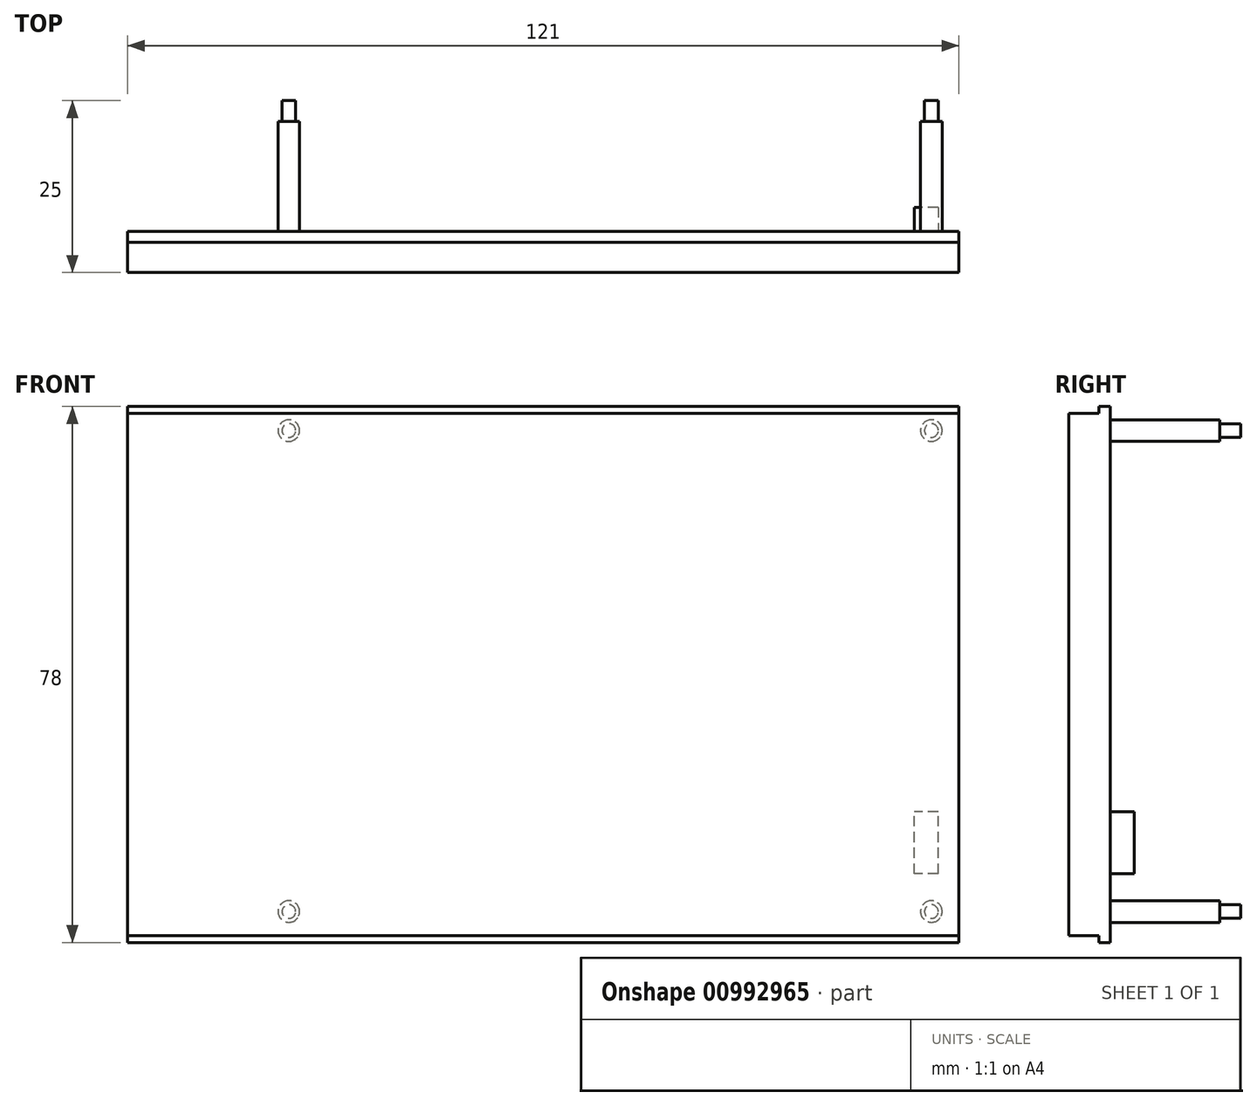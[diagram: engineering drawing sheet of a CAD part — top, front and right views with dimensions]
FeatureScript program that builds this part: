
annotation { "Feature Type Name" : "Feature", "Feature Type Description" : "" }
export const myFeature = defineFeature(function(context is Context, id is Id, definition is map)
    precondition{}
    {
        {
            var Q0;
            Q0=qCreatedBy(makeId("Front.planeOp"),FACE);
            var sketch = newSketch(context, id + "F0", { "sketchPlane" : qUnion([Q0])});
            skLineSegment(sketch, "E0.bottom", {"start": v(60.5, 38) * mm, "end": v(-60.5, 38) * mm});
            skLineSegment(sketch, "E0.top", {"start": v(60.5, -38) * mm, "end": v(-60.5, -38) * mm});
            skLineSegment(sketch, "E0.left", {"start": v(60.5, 38) * mm, "end": v(60.5, -38) * mm});
            skLineSegment(sketch, "E0.right", {"start": v(-60.5, 38) * mm, "end": v(-60.5, -38) * mm});
            skPoint(sketch, "E0.middle", {"position": v(0, 0) * mm});
            skSolve(sketch);
        }
        {
            var Q0;
            Q0=makeQuery(id+"F0.imprint","IMPRINT",FACE,{"disambiguationData":[TD([[makeQuery(id+"F0.imprint","IMPRINT",EDGE,{"derivedFrom":sQuery(id+"F0.wireOp",EDGE,"E0.bottom")}),1.0]])]});
            extrude(context, id + "F1", {"entities" : qUnion([Q0]), "depth" : 6 * mm, "offsetDistance" : 25.4 * mm});
        }
        {
            var Q0;
            Q0=qCreatedBy(makeId("Front.planeOp"),FACE);
            var sketch = newSketch(context, id + "F2", { "sketchPlane" : qUnion([Q0])});
            skLineSegment(sketch, "E1.bottom", {"start": v(-60.5, 39) * mm, "end": v(60.5, 39) * mm});
            skLineSegment(sketch, "E1.top", {"start": v(-60.5, -39) * mm, "end": v(60.5, -39) * mm});
            skLineSegment(sketch, "E1.left", {"start": v(-60.5, 39) * mm, "end": v(-60.5, -39) * mm});
            skLineSegment(sketch, "E1.right", {"start": v(60.5, 39) * mm, "end": v(60.5, -39) * mm});
            skPoint(sketch, "E1.middle", {"position": v(0, 0) * mm});
            skSolve(sketch);
        }
        {
            var Q0;
            Q0=makeQuery(id+"F2.imprint","IMPRINT",FACE,{"disambiguationData":[TD([[makeQuery(id+"F2.imprint","IMPRINT",EDGE,{"derivedFrom":sQuery(id+"F2.wireOp",EDGE,"E1.bottom")}),-1.0]])]});
            extrude(context, id + "F3", {"entities" : qUnion([Q0]), "operationType" : NewBodyOperationType.ADD, "depth" : 1.6 * mm, "offsetDistance" : 25.4 * mm});
        }
        {
            var Q0;
            Q0=makeQuery(id+"F3.boolean.opBoolean","MERGE",FACE,{"derivedFrom":[makeQuery(id+"F1.opExtrude","CAP_FACE",FACE,{"disambiguationData":[OSD([sQuery(id+"F0.wireOp",EDGE,"E0.bottom"),sQuery(id+"F0.wireOp",EDGE,"E0.top"),sQuery(id+"F0.wireOp",EDGE,"E0.left"),sQuery(id+"F0.wireOp",EDGE,"E0.right")])],"isStart":true}),makeQuery(id+"F3.opExtrude","CAP_FACE",FACE,{"disambiguationData":[OSD([sQuery(id+"F2.wireOp",EDGE,"E1.bottom"),sQuery(id+"F2.wireOp",EDGE,"E1.top"),sQuery(id+"F2.wireOp",EDGE,"E1.left"),sQuery(id+"F2.wireOp",EDGE,"E1.right")])],"isStart":true})]});
            var sketch = newSketch(context, id + "F4", { "sketchPlane" : qUnion([Q0])});
            skCircle(sketch, "E2", {"center": v(-56.5, 35.5) * mm, "radius": 1 * mm});
            skCircle(sketch, "E3", {"center": v(-56.5, -34.5) * mm, "radius": 1 * mm});
            skCircle(sketch, "E4", {"center": v(37, -34.5) * mm, "radius": 1 * mm});
            skCircle(sketch, "E5", {"center": v(37, 35.5) * mm, "radius": 1 * mm});
            skSolve(sketch);
        }
        {
            var Q0;
            Q0 = qSketchRegion(id + "F4", true);
            extrude(context, id + "F5", {"entities" : qUnion([Q0]), "operationType" : NewBodyOperationType.ADD, "depth" : 2 * mm, "offsetDistance" : 25.4 * mm});
        }
        {
            var Q0;
            Q0=makeQuery(id+"F3.boolean.opBoolean","MERGE",FACE,{"derivedFrom":[makeQuery(id+"F1.opExtrude","CAP_FACE",FACE,{"disambiguationData":[OSD([sQuery(id+"F0.wireOp",EDGE,"E0.bottom"),sQuery(id+"F0.wireOp",EDGE,"E0.top"),sQuery(id+"F0.wireOp",EDGE,"E0.left"),sQuery(id+"F0.wireOp",EDGE,"E0.right")])],"isStart":true}),makeQuery(id+"F3.opExtrude","CAP_FACE",FACE,{"disambiguationData":[OSD([sQuery(id+"F2.wireOp",EDGE,"E1.bottom"),sQuery(id+"F2.wireOp",EDGE,"E1.top"),sQuery(id+"F2.wireOp",EDGE,"E1.left"),sQuery(id+"F2.wireOp",EDGE,"E1.right")])],"isStart":true})]});
            var sketch = newSketch(context, id + "F6", { "sketchPlane" : qUnion([Q0])});
            skLineSegment(sketch, "E6.bottom", {"start": v(-57.5, -29) * mm, "end": v(-54, -29) * mm});
            skLineSegment(sketch, "E6.top", {"start": v(-57.5, -20) * mm, "end": v(-54, -20) * mm});
            skLineSegment(sketch, "E6.left", {"start": v(-57.5, -29) * mm, "end": v(-57.5, -20) * mm});
            skLineSegment(sketch, "E6.right", {"start": v(-54, -29) * mm, "end": v(-54, -20) * mm});
            skSolve(sketch);
        }
        {
            var Q0;
            Q0=makeQuery(id+"F6.imprint","IMPRINT",FACE,{"disambiguationData":[TD([[makeQuery(id+"F6.imprint","IMPRINT",EDGE,{"derivedFrom":sQuery(id+"F6.wireOp",EDGE,"E6.bottom")}),1.0]])]});
            extrude(context, id + "F7", {"entities" : qUnion([Q0]), "operationType" : NewBodyOperationType.ADD, "depth" : 3.5 * mm, "offsetDistance" : 25.4 * mm});
        }
        {
            var Q0;
            Q0=makeQuery(id+"F3.boolean.opBoolean","MERGE",FACE,{"derivedFrom":[makeQuery(id+"F1.opExtrude","CAP_FACE",FACE,{"disambiguationData":[OSD([sQuery(id+"F0.wireOp",EDGE,"E0.bottom"),sQuery(id+"F0.wireOp",EDGE,"E0.top"),sQuery(id+"F0.wireOp",EDGE,"E0.left"),sQuery(id+"F0.wireOp",EDGE,"E0.right")])],"isStart":true}),makeQuery(id+"F3.opExtrude","CAP_FACE",FACE,{"disambiguationData":[OSD([sQuery(id+"F2.wireOp",EDGE,"E1.bottom"),sQuery(id+"F2.wireOp",EDGE,"E1.top"),sQuery(id+"F2.wireOp",EDGE,"E1.left"),sQuery(id+"F2.wireOp",EDGE,"E1.right")])],"isStart":true})]});
            var sketch = newSketch(context, id + "F8", { "sketchPlane" : qUnion([Q0])});
            skCircle(sketch, "E7", {"center": v(-56.5, 35.5) * mm, "radius": 1.57 * mm});
            skCircle(sketch, "E8", {"center": v(37, 35.5) * mm, "radius": 1.57 * mm});
            skCircle(sketch, "E9", {"center": v(-56.5, -34.5) * mm, "radius": 1.57 * mm});
            skCircle(sketch, "E10", {"center": v(37, -34.5) * mm, "radius": 1.57 * mm});
            skSolve(sketch);
        }
        {
            var Q0;
            Q0 = qSketchRegion(id + "F8", true);
            extrude(context, id + "F9", {"entities" : qUnion([Q0]), "operationType" : NewBodyOperationType.ADD, "depth" : 16 * mm, "offsetDistance" : 25.4 * mm});
        }
        {
            var Q0;
            Q0=makeQuery(id+"F3.boolean.opBoolean","MERGE",FACE,{"derivedFrom":[makeQuery(id+"F1.opExtrude","CAP_FACE",FACE,{"disambiguationData":[OSD([sQuery(id+"F0.wireOp",EDGE,"E0.bottom"),sQuery(id+"F0.wireOp",EDGE,"E0.top"),sQuery(id+"F0.wireOp",EDGE,"E0.left"),sQuery(id+"F0.wireOp",EDGE,"E0.right")])],"isStart":true}),makeQuery(id+"F3.opExtrude","CAP_FACE",FACE,{"disambiguationData":[OSD([sQuery(id+"F2.wireOp",EDGE,"E1.bottom"),sQuery(id+"F2.wireOp",EDGE,"E1.top"),sQuery(id+"F2.wireOp",EDGE,"E1.left"),sQuery(id+"F2.wireOp",EDGE,"E1.right")])],"isStart":true})]});
            var sketch = newSketch(context, id + "F10", { "sketchPlane" : qUnion([Q0])});
            skCircle(sketch, "E11", {"center": v(37, 35.5) * mm, "radius": 1 * mm});
            skCircle(sketch, "E12", {"center": v(37, -34.5) * mm, "radius": 1 * mm});
            skCircle(sketch, "E13", {"center": v(-56.5, -34.5) * mm, "radius": 1 * mm});
            skCircle(sketch, "E14", {"center": v(-56.5, 35.5) * mm, "radius": 1 * mm});
            skSolve(sketch);
        }
        {
            var Q0;
            Q0 = qSketchRegion(id + "F10", true);
            extrude(context, id + "F11", {"entities" : qUnion([Q0]), "operationType" : NewBodyOperationType.ADD, "depth" : 19 * mm, "offsetDistance" : 25.4 * mm});
        }
    });
